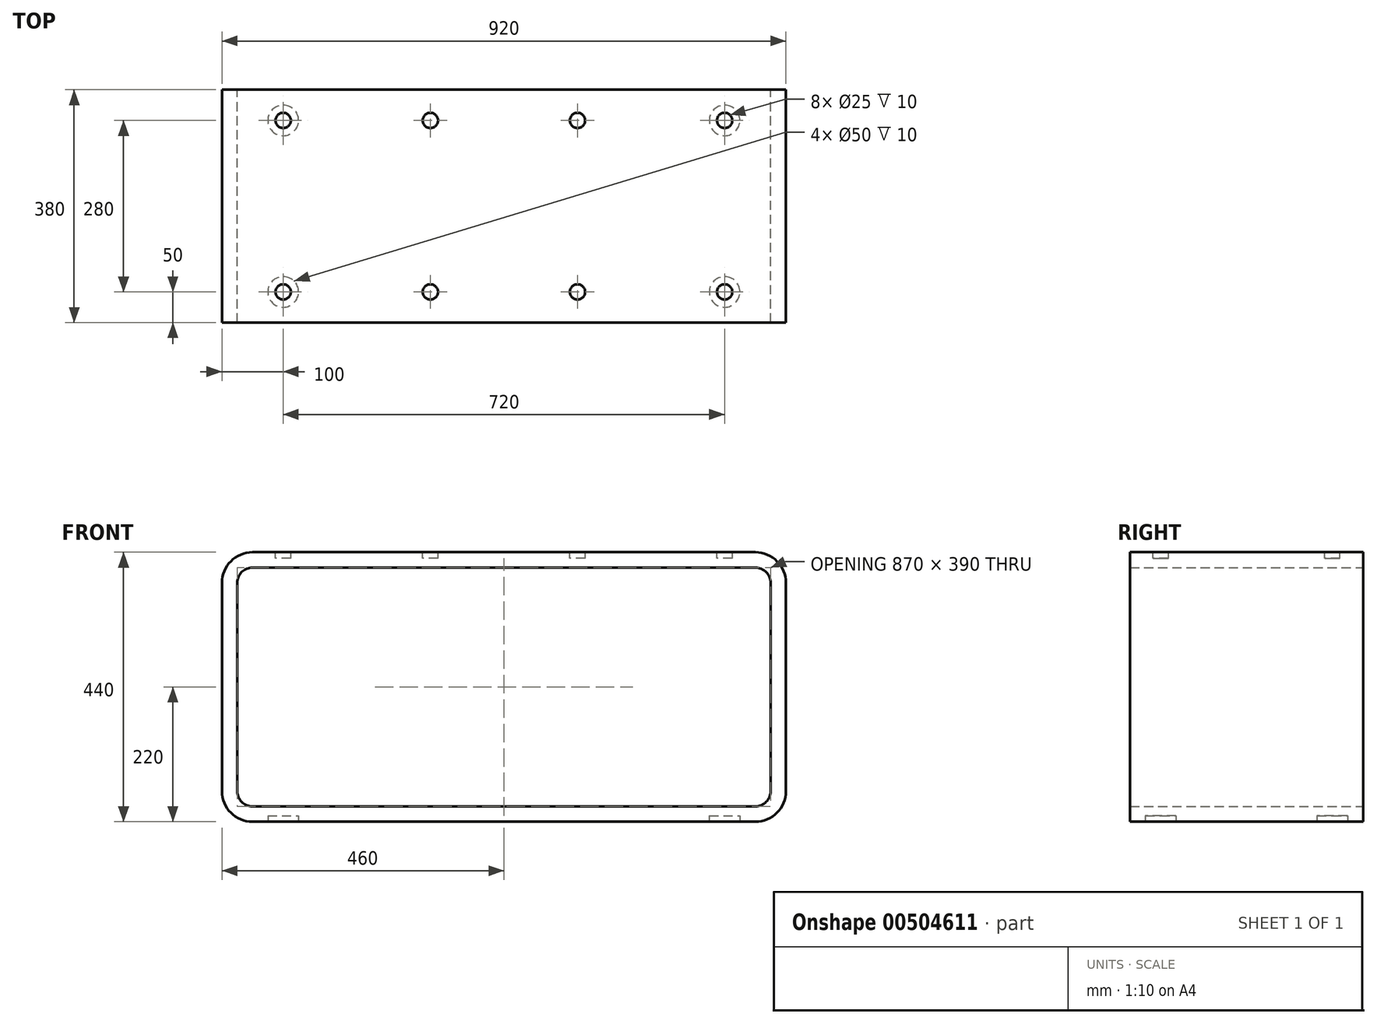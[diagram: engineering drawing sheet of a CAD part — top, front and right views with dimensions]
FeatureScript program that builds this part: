
annotation { "Feature Type Name" : "Feature", "Feature Type Description" : "" }
export const myFeature = defineFeature(function(context is Context, id is Id, definition is map)
    precondition{}
    {
        {
            var Q0;
            Q0=qCreatedBy(makeId("Front.planeOp"),FACE);
            var sketch = newSketch(context, id + "F0", { "sketchPlane" : qUnion([Q0])});
            skLineSegment(sketch, "E0.bottom", {"start": v(410, -220) * mm, "end": v(-410, -220) * mm});
            skLineSegment(sketch, "E0.top", {"start": v(410, 220) * mm, "end": v(-410, 220) * mm});
            skLineSegment(sketch, "E0.left", {"start": v(460, -170) * mm, "end": v(460, 170) * mm});
            skLineSegment(sketch, "E0.right", {"start": v(-460, -170) * mm, "end": v(-460, 170) * mm});
            skPoint(sketch, "E0.middle", {"position": v(0, 0) * mm});
            skPoint(sketch, "E1.visualSharp", {"position": v(-460, 220) * mm});
            skArc(sketch, "E1.filletArc", {"start": v(-410, 220) * mm, "mid": v(-445.36, 205.36) * mm, "end": v(-460, 170) * mm});
            skPoint(sketch, "E2.visualSharp", {"position": v(-460, -220) * mm});
            skArc(sketch, "E2.filletArc", {"start": v(-460, -170) * mm, "mid": v(-445.36, -205.36) * mm, "end": v(-410, -220) * mm});
            skPoint(sketch, "E3.visualSharp", {"position": v(460, -220) * mm});
            skArc(sketch, "E3.filletArc", {"start": v(410, -220) * mm, "mid": v(445.36, -205.36) * mm, "end": v(460, -170) * mm});
            skPoint(sketch, "E4.visualSharp", {"position": v(460, 220) * mm});
            skArc(sketch, "E4.filletArc", {"start": v(460, 170) * mm, "mid": v(445.36, 205.36) * mm, "end": v(410, 220) * mm});
            skArc(sketch, "E5.0", {"start": v(410, -195) * mm, "mid": v(427.68, -187.68) * mm, "end": v(435, -170) * mm});
            skLineSegment(sketch, "E5.1", {"start": v(435, -170) * mm, "end": v(435, 170) * mm});
            skLineSegment(sketch, "E5.2", {"start": v(410, -195) * mm, "end": v(-410, -195) * mm});
            skArc(sketch, "E5.3", {"start": v(435, 170) * mm, "mid": v(427.68, 187.68) * mm, "end": v(410, 195) * mm});
            skArc(sketch, "E5.4", {"start": v(-435, -170) * mm, "mid": v(-427.68, -187.68) * mm, "end": v(-410, -195) * mm});
            skLineSegment(sketch, "E5.5", {"start": v(-435, -170) * mm, "end": v(-435, 170) * mm});
            skArc(sketch, "E5.6", {"start": v(-410, 195) * mm, "mid": v(-427.68, 187.68) * mm, "end": v(-435, 170) * mm});
            skLineSegment(sketch, "E5.7", {"start": v(410, 195) * mm, "end": v(-410, 195) * mm});
            skSolve(sketch);
        }
        {
            var Q0;
            Q0=makeQuery(id+"F0.imprint","IMPRINT",FACE,{"disambiguationData":[TD([[makeQuery(id+"F0.imprint","IMPRINT",EDGE,{"derivedFrom":sQuery(id+"F0.wireOp",EDGE,"E0.bottom")}),-1.0]])]});
            extrude(context, id + "F1", {"entities" : qUnion([Q0]), "depth" : 380 * mm});
        }
        {
            var Q0;
            Q0=makeQuery(id+"F1.opExtrude","SWEPT_FACE",FACE,{"disambiguationData":[OSD([sQuery(id+"F0.wireOp",EDGE,"E0.bottom")])]});
            var sketch = newSketch(context, id + "F2", { "sketchPlane" : qUnion([Q0])});
            skCircle(sketch, "E6", {"center": v(-360, 330) * mm, "radius": 25 * mm});
            skCircle(sketch, "E7", {"center": v(-360, 50) * mm, "radius": 25 * mm});
            skCircle(sketch, "E8", {"center": v(360, 330) * mm, "radius": 25 * mm});
            skCircle(sketch, "E9", {"center": v(360, 50) * mm, "radius": 25 * mm});
            skSolve(sketch);
        }
        {
            var Q0;
            Q0=makeQuery(id+"F2.imprint","IMPRINT",FACE,{"disambiguationData":[TD([[makeQuery(id+"F2.imprint","IMPRINT",EDGE,{"derivedFrom":sQuery(id+"F2.wireOp",EDGE,"E7")}),1.0]])]});
            var Q1;
            Q1=makeQuery(id+"F2.imprint","IMPRINT",FACE,{"disambiguationData":[TD([[makeQuery(id+"F2.imprint","IMPRINT",EDGE,{"derivedFrom":sQuery(id+"F2.wireOp",EDGE,"E6")}),1.0]])]});
            var Q2;
            Q2=makeQuery(id+"F2.imprint","IMPRINT",FACE,{"disambiguationData":[TD([[makeQuery(id+"F2.imprint","IMPRINT",EDGE,{"derivedFrom":sQuery(id+"F2.wireOp",EDGE,"E8")}),1.0]])]});
            var Q3;
            Q3=makeQuery(id+"F2.imprint","IMPRINT",FACE,{"disambiguationData":[TD([[makeQuery(id+"F2.imprint","IMPRINT",EDGE,{"derivedFrom":sQuery(id+"F2.wireOp",EDGE,"E9")}),1.0]])]});
            extrude(context, id + "F3", {"entities" : qUnion([Q0, Q1, Q2, Q3]), "operationType" : NewBodyOperationType.REMOVE, "oppositeDirection" : true, "depth" : 10 * mm});
        }
        {
            var Q0;
            Q0=makeQuery(id+"F1.opExtrude","SWEPT_FACE",FACE,{"disambiguationData":[OSD([sQuery(id+"F0.wireOp",EDGE,"E0.top")])]});
            var sketch = newSketch(context, id + "F4", { "sketchPlane" : qUnion([Q0])});
            skCircle(sketch, "E10", {"center": v(-360, -50) * mm, "radius": 12.5 * mm});
            skCircle(sketch, "E11", {"center": v(-360, -330) * mm, "radius": 12.5 * mm});
            skPoint(sketch, "E12.centerSnap0", {"position": v(0, -380) * mm});
            skCircle(sketch, "E13", {"center": v(-120, -330) * mm, "radius": 12.5 * mm});
            skCircle(sketch, "E14", {"center": v(-120, -50) * mm, "radius": 12.5 * mm});
            skCircle(sketch, "E15", {"center": v(360, -330) * mm, "radius": 12.5 * mm});
            skCircle(sketch, "E16", {"center": v(120, -330) * mm, "radius": 12.5 * mm});
            skCircle(sketch, "E17", {"center": v(360, -50) * mm, "radius": 12.5 * mm});
            skCircle(sketch, "E18", {"center": v(120, -50) * mm, "radius": 12.5 * mm});
            skSolve(sketch);
        }
        {
            var Q0;
            Q0=makeQuery(id+"F4.imprint","IMPRINT",FACE,{"disambiguationData":[TD([[makeQuery(id+"F4.imprint","IMPRINT",EDGE,{"derivedFrom":sQuery(id+"F4.wireOp",EDGE,"E10")}),1.0]])]});
            var Q1;
            Q1=makeQuery(id+"F4.imprint","IMPRINT",FACE,{"disambiguationData":[TD([[makeQuery(id+"F4.imprint","IMPRINT",EDGE,{"derivedFrom":sQuery(id+"F4.wireOp",EDGE,"E11")}),1.0]])]});
            var Q2;
            Q2=makeQuery(id+"F4.imprint","IMPRINT",FACE,{"disambiguationData":[TD([[makeQuery(id+"F4.imprint","IMPRINT",EDGE,{"derivedFrom":sQuery(id+"F4.wireOp",EDGE,"E13")}),1.0]])]});
            var Q3;
            Q3=makeQuery(id+"F4.imprint","IMPRINT",FACE,{"disambiguationData":[TD([[makeQuery(id+"F4.imprint","IMPRINT",EDGE,{"derivedFrom":sQuery(id+"F4.wireOp",EDGE,"E14")}),1.0]])]});
            var Q4;
            Q4=makeQuery(id+"F4.imprint","IMPRINT",FACE,{"disambiguationData":[TD([[makeQuery(id+"F4.imprint","IMPRINT",EDGE,{"derivedFrom":sQuery(id+"F4.wireOp",EDGE,"E16")}),1.0]])]});
            var Q5;
            Q5=makeQuery(id+"F4.imprint","IMPRINT",FACE,{"disambiguationData":[TD([[makeQuery(id+"F4.imprint","IMPRINT",EDGE,{"derivedFrom":sQuery(id+"F4.wireOp",EDGE,"E18")}),1.0]])]});
            var Q6;
            Q6=makeQuery(id+"F4.imprint","IMPRINT",FACE,{"disambiguationData":[TD([[makeQuery(id+"F4.imprint","IMPRINT",EDGE,{"derivedFrom":sQuery(id+"F4.wireOp",EDGE,"E15")}),1.0]])]});
            var Q7;
            Q7=makeQuery(id+"F4.imprint","IMPRINT",FACE,{"disambiguationData":[TD([[makeQuery(id+"F4.imprint","IMPRINT",EDGE,{"derivedFrom":sQuery(id+"F4.wireOp",EDGE,"E17")}),1.0]])]});
            extrude(context, id + "F5", {"entities" : qUnion([Q0, Q1, Q2, Q3, Q4, Q5, Q6, Q7]), "operationType" : NewBodyOperationType.REMOVE, "oppositeDirection" : true, "depth" : 10 * mm});
        }
    });
